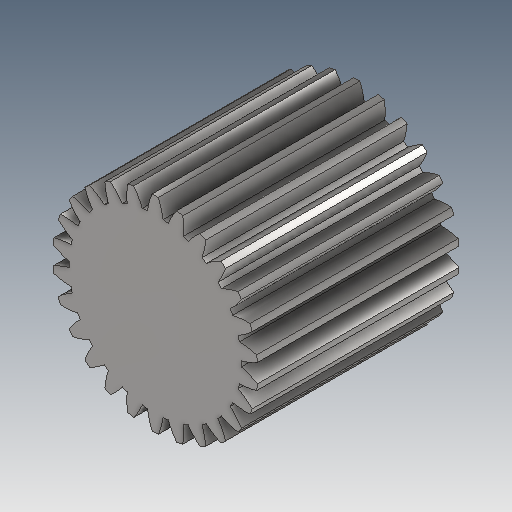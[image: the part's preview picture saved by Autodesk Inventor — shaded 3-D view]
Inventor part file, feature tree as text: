
AUTODESK INVENTOR PART (.ipt)
format: ipt  version: 2025 (Build 290162000, 162)  size: 320,000 bytes
history: native  units: mm (DEFAULTED — no unit token found)
features: plane x3, other x2, extrude x1, sketch x1
ambient origin geometry x8: Origin, YZ Plane, XZ Plane, XY Plane, X Axis, Y Axis, Z Axis, Center Point
bodies: Solid1 (feature_tree)
feature tree (7):
  extrude  "Extrusion1"  Depth=55.0mm TaperAngle=0.0deg
  plane  "Work Plane2"
  plane  "Work Plane8"
  plane  "Work Plane9"
  other  "正齿轮"
  sketch  "Sketch1"  dims[d0=56.0mm d1=55.0mm d2=0.0mm d3=52.0mm d4=10.0mm d5=0.0mm d16=146.0mm d17=0.0mm d34=1.208305mm d39=0.0mm d41=0.0mm d43=146.0mm d46=146.0mm d47=0.0mm d48=0.0mm]
  other  "Srf1"
